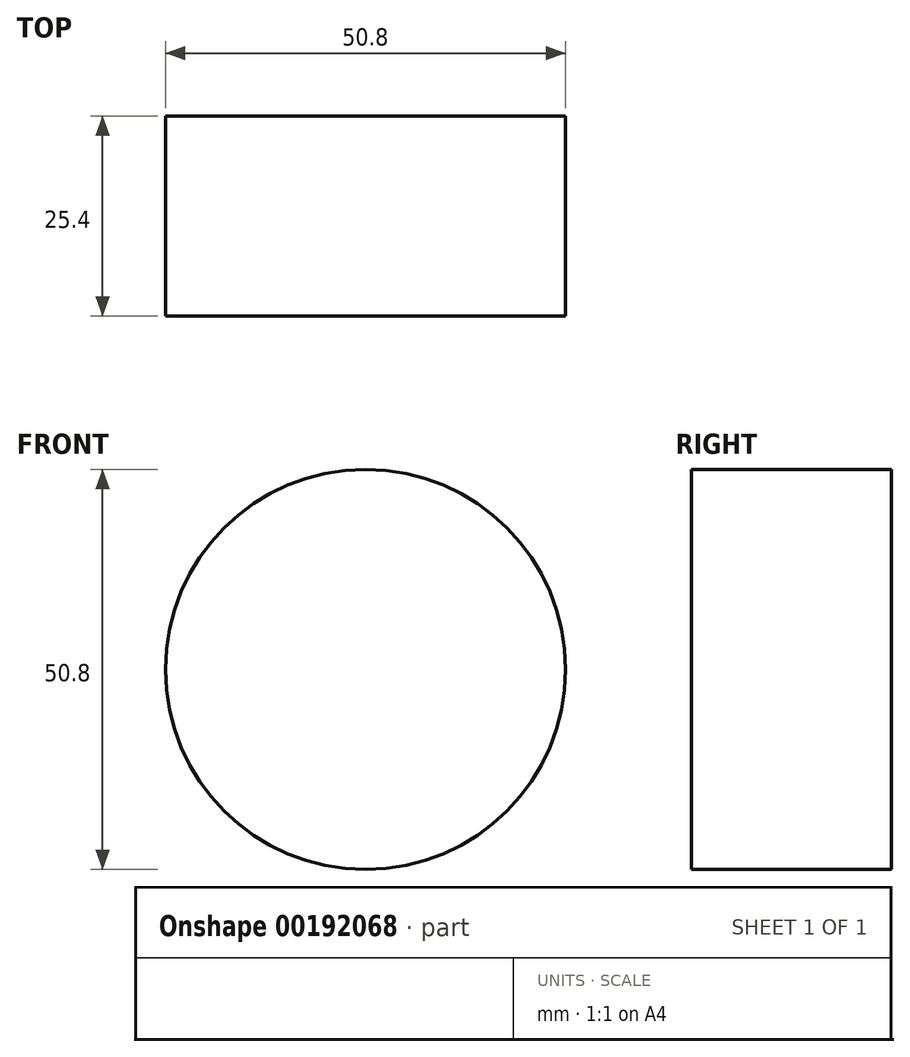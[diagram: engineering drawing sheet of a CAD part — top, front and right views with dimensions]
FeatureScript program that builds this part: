
annotation { "Feature Type Name" : "Feature", "Feature Type Description" : "" }
export const myFeature = defineFeature(function(context is Context, id is Id, definition is map)
    precondition{}
    {
        {
            var Q0;
            Q0=qCreatedBy(makeId("Front.planeOp"),FACE);
            var sketch = newSketch(context, id + "F0", { "sketchPlane" : qUnion([Q0])});
            skCircle(sketch, "E0", {"center": v(0, 0) * mm, "radius": 25.4 * mm});
            skSolve(sketch);
        }
        {
            var Q0;
            Q0=makeQuery(id+"F0.imprint","IMPRINT",FACE,{"disambiguationData":[TD([[makeQuery(id+"F0.imprint","IMPRINT",EDGE,{"derivedFrom":sQuery(id+"F0.wireOp",EDGE,"E0")}),1.0]])]});
            extrude(context, id + "F1", {"entities" : qUnion([Q0]), "depth" : 25.4 * mm});
        }
    });
